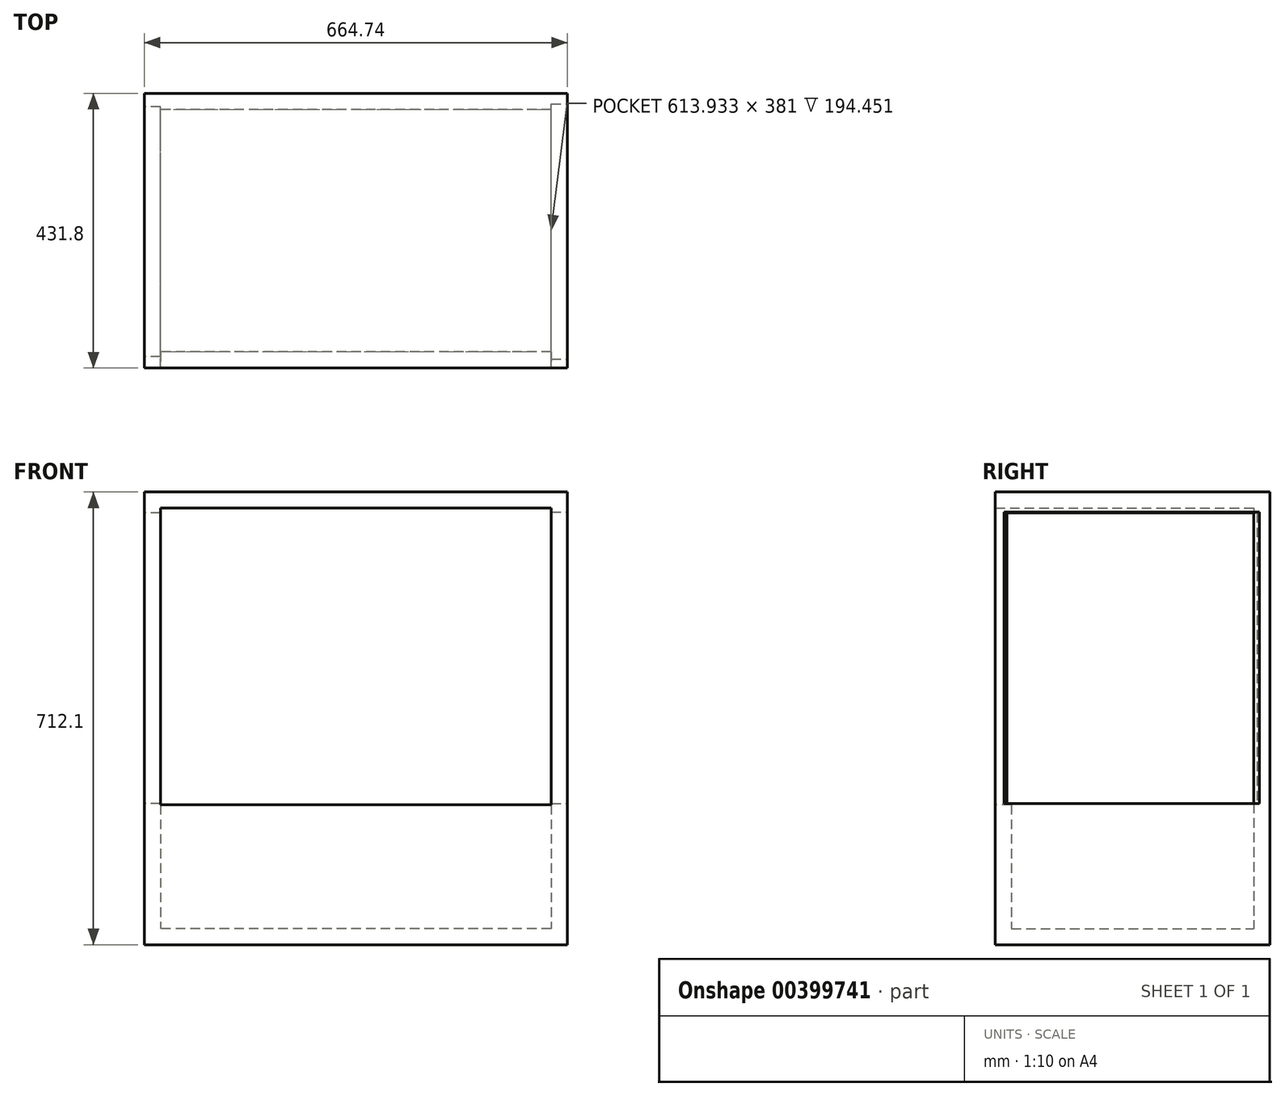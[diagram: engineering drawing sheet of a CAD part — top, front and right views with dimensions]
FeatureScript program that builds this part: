
annotation { "Feature Type Name" : "Feature", "Feature Type Description" : "" }
export const myFeature = defineFeature(function(context is Context, id is Id, definition is map)
    precondition{}
    {
        {
            var Q0;
            Q0=qCreatedBy(makeId("Front.planeOp"),FACE);
            var sketch = newSketch(context, id + "F0", { "sketchPlane" : qUnion([Q0])});
            skLineSegment(sketch, "E0.bottom", {"start": v(332.37, 356.05) * mm, "end": v(-332.37, 356.05) * mm});
            skLineSegment(sketch, "E0.top", {"start": v(332.37, -356.05) * mm, "end": v(-332.37, -356.05) * mm});
            skLineSegment(sketch, "E0.left", {"start": v(332.37, 356.05) * mm, "end": v(332.37, -356.05) * mm});
            skLineSegment(sketch, "E0.right", {"start": v(-332.37, 356.05) * mm, "end": v(-332.37, -356.05) * mm});
            skPoint(sketch, "E0.middle", {"position": v(0, 0) * mm});
            skSolve(sketch);
        }
        {
            var Q0;
            Q0=makeQuery(id+"F0.imprint","IMPRINT",FACE,{"disambiguationData":[TD([[makeQuery(id+"F0.imprint","IMPRINT",EDGE,{"derivedFrom":sQuery(id+"F0.wireOp",EDGE,"E0.bottom")}),1.0]])]});
            extrude(context, id + "F1", {"entities" : qUnion([Q0]), "depth" : 431.8 * mm});
        }
        {
            var Q0;
            Q0=makeQuery(id+"F1.opExtrude","CAP_FACE",FACE,{"disambiguationData":[OSD([sQuery(id+"F0.wireOp",EDGE,"E0.bottom"),sQuery(id+"F0.wireOp",EDGE,"E0.top"),sQuery(id+"F0.wireOp",EDGE,"E0.left"),sQuery(id+"F0.wireOp",EDGE,"E0.right")])],"isStart":false});
            shell(context, id + "F2", {"entities" : qUnion([Q0]), "thickness" : 25.4 * mm});
        }
        {
            var Q0;
            Q0=makeQuery(id+"F1.opExtrude","CAP_FACE",FACE,{"disambiguationData":[OSD([sQuery(id+"F0.wireOp",EDGE,"E0.bottom"),sQuery(id+"F0.wireOp",EDGE,"E0.top"),sQuery(id+"F0.wireOp",EDGE,"E0.left"),sQuery(id+"F0.wireOp",EDGE,"E0.right")])],"isStart":false});
            var sketch = newSketch(context, id + "F3", { "sketchPlane" : qUnion([Q0])});
            skLineSegment(sketch, "E1.bottom", {"start": v(-332.37, -136.2) * mm, "end": v(332.37, -136.2) * mm});
            skLineSegment(sketch, "E1.top", {"start": v(-332.37, -356.05) * mm, "end": v(332.37, -356.05) * mm});
            skLineSegment(sketch, "E1.left", {"start": v(-332.37, -136.2) * mm, "end": v(-332.37, -356.05) * mm});
            skLineSegment(sketch, "E1.right", {"start": v(332.37, -136.2) * mm, "end": v(332.37, -356.05) * mm});
            skSolve(sketch);
        }
        {
            var Q0;
            {var subQ7=sQuery(id+"F0.wireOp",EDGE,"E0.top");var subQ8=makeQuery(id+"F2.opShell","OFFSET_EDGE",EDGE,{"disambiguationData":[OSD([subQ7]),TDD([makeQuery(id+"F1.opExtrude","CAP_EDGE",EDGE,{"disambiguationData":[OSD([subQ7])],"isStart":false})])]});Q0=makeQuery(id+"F3.imprint","IMPRINT",FACE,{"disambiguationData":[TD([[makeQuery(id+"F3.imprint","IMPRINT",EDGE,{"derivedFrom":subQ8}),-1.0]])]});}
            extrude(context, id + "F4", {"entities" : qUnion([Q0]), "operationType" : NewBodyOperationType.ADD, "oppositeDirection" : true, "depth" : 25.4 * mm});
        }
        {
            var Q0;
            Q0=makeQuery(id+"F1.opExtrude","SWEPT_FACE",FACE,{"disambiguationData":[OSD([sQuery(id+"F0.wireOp",EDGE,"E0.left")])]});
            var sketch = newSketch(context, id + "F5", { "sketchPlane" : qUnion([Q0])});
            skLineSegment(sketch, "E2.bottom", {"start": v(-418, 324.33) * mm, "end": v(-16.64, 324.33) * mm});
            skLineSegment(sketch, "E2.top", {"start": v(-418, -144.48) * mm, "end": v(-16.64, -144.48) * mm});
            skLineSegment(sketch, "E2.left", {"start": v(-418, 324.33) * mm, "end": v(-418, -144.48) * mm});
            skLineSegment(sketch, "E2.right", {"start": v(-16.64, 324.33) * mm, "end": v(-16.64, -144.48) * mm});
            skSolve(sketch);
        }
        {
            var Q0;
            Q0=makeQuery(id+"F5.imprint","IMPRINT",FACE,{"disambiguationData":[TD([[makeQuery(id+"F5.imprint","IMPRINT",EDGE,{"derivedFrom":sQuery(id+"F5.wireOp",EDGE,"E2.bottom")}),-1.0]])]});
            extrude(context, id + "F6", {"entities" : qUnion([Q0]), "operationType" : NewBodyOperationType.REMOVE, "oppositeDirection" : true, "depth" : 25.4 * mm});
        }
        {
            var Q0;
            Q0=makeQuery(id+"F1.opExtrude","SWEPT_FACE",FACE,{"disambiguationData":[OSD([sQuery(id+"F0.wireOp",EDGE,"E0.right")])]});
            var sketch = newSketch(context, id + "F7", { "sketchPlane" : qUnion([Q0])});
            skLineSegment(sketch, "E3.bottom", {"start": v(413.69, 322.89) * mm, "end": v(20.74, 322.89) * mm});
            skLineSegment(sketch, "E3.top", {"start": v(413.69, -134.3) * mm, "end": v(20.74, -134.3) * mm});
            skLineSegment(sketch, "E3.left", {"start": v(413.69, 322.89) * mm, "end": v(413.69, -134.3) * mm});
            skLineSegment(sketch, "E3.right", {"start": v(20.74, 322.89) * mm, "end": v(20.74, -134.3) * mm});
            skSolve(sketch);
        }
        {
            var Q0;
            Q0=makeQuery(id+"F7.imprint","IMPRINT",FACE,{"disambiguationData":[TD([[makeQuery(id+"F7.imprint","IMPRINT",EDGE,{"derivedFrom":sQuery(id+"F7.wireOp",EDGE,"E3.bottom")}),1.0]])]});
            extrude(context, id + "F8", {"entities" : qUnion([Q0]), "operationType" : NewBodyOperationType.REMOVE, "oppositeDirection" : true, "depth" : 25.4 * mm});
        }
        {
            var Q0;
            Q0=makeQuery(id+"F6.boolean.opBoolean","COPY",FACE,{"derivedFrom":makeQuery(id+"F6.opExtrude","SWEPT_FACE",FACE,{"disambiguationData":[OSD([sQuery(id+"F5.wireOp",EDGE,"E2.top")])]})});
            extrude(context, id + "F9", {"entities" : qUnion([Q0]), "operationType" : NewBodyOperationType.ADD, "depth" : 10.67 * mm});
        }
    });
